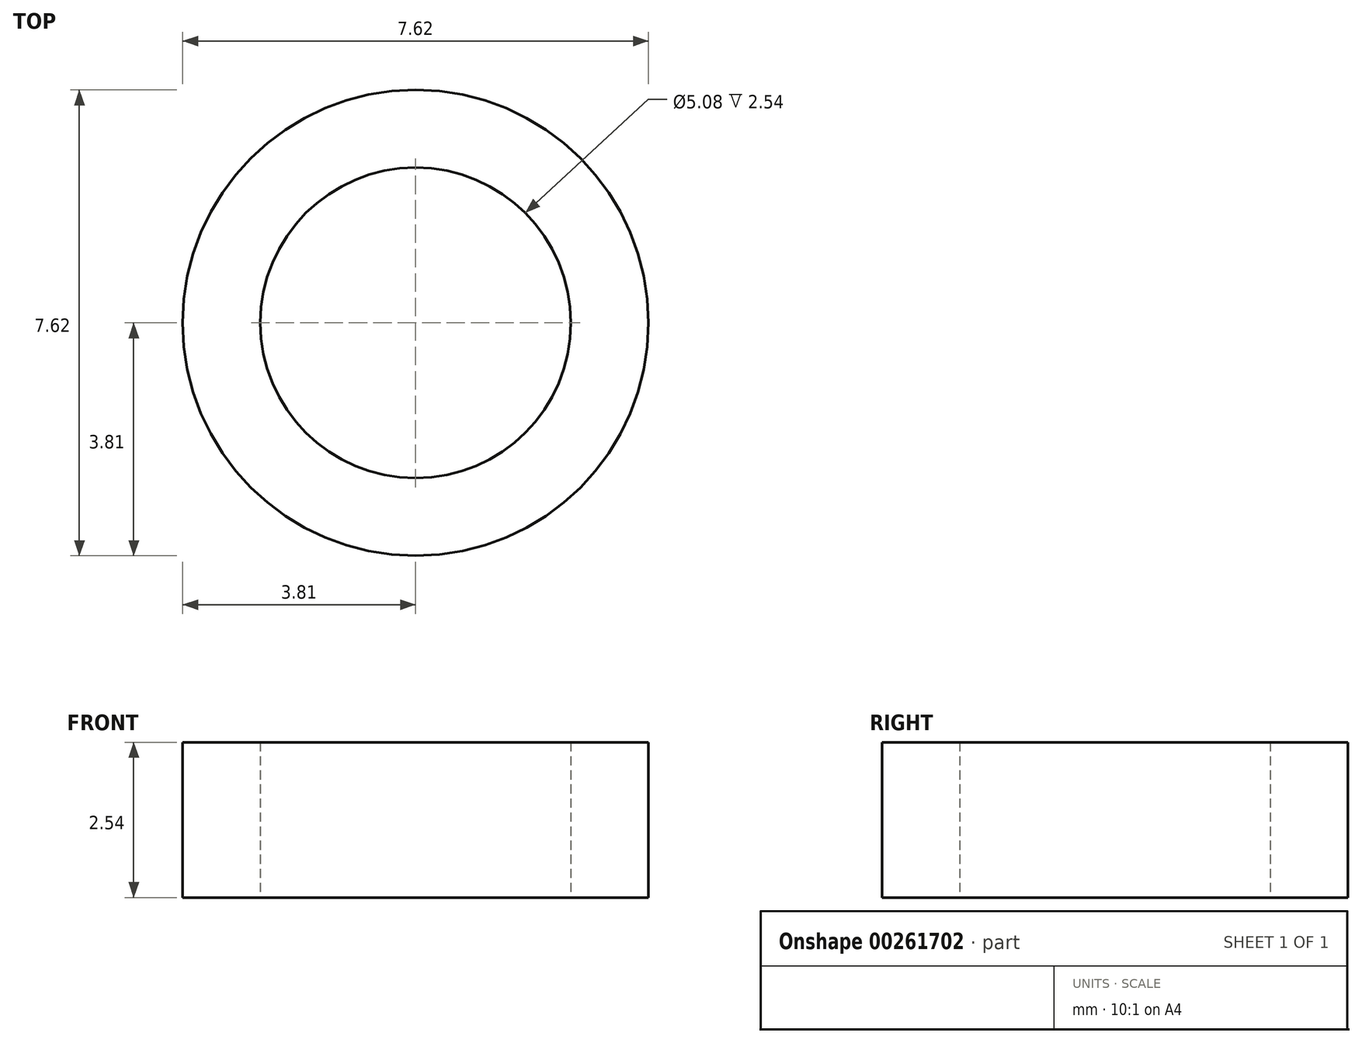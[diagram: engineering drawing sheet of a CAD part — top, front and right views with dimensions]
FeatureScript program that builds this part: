
annotation { "Feature Type Name" : "Feature", "Feature Type Description" : "" }
export const myFeature = defineFeature(function(context is Context, id is Id, definition is map)
    precondition{}
    {
        {
            var Q0;
            Q0=qCreatedBy(makeId("Top.planeOp"),FACE);
            var sketch = newSketch(context, id + "F0", { "sketchPlane" : qUnion([Q0])});
            skCircle(sketch, "E0", {"center": v(0, 0) * mm, "radius": 3.81 * mm});
            skCircle(sketch, "E1", {"center": v(0, 0) * mm, "radius": 2.54 * mm});
            skSolve(sketch);
        }
        {
            var Q0;
            Q0 = qSketchRegion(id + "F0", true);
            extrude(context, id + "F1", {"entities" : qUnion([Q0]), "depth" : 2.54 * mm});
        }
    });
